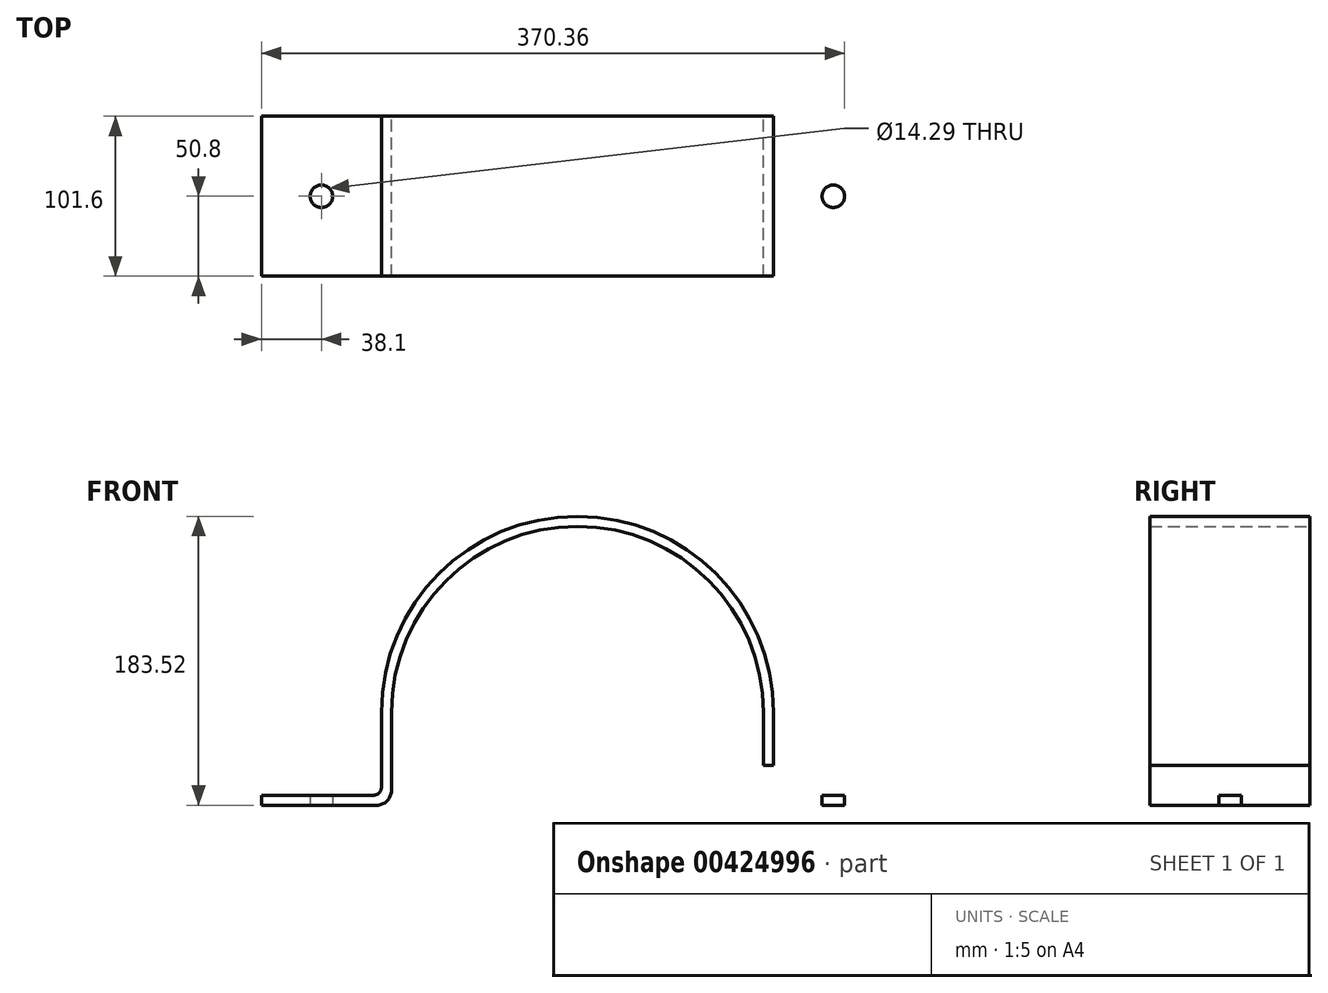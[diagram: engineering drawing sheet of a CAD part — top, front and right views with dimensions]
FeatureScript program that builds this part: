
annotation { "Feature Type Name" : "Feature", "Feature Type Description" : "" }
export const myFeature = defineFeature(function(context is Context, id is Id, definition is map)
    precondition{}
    {
        {
            var Q0;
            Q0=qCreatedBy(makeId("Front.planeOp"),FACE);
            var sketch = newSketch(context, id + "F0", { "sketchPlane" : qUnion([Q0])});
            skArc(sketch, "E0", {"start": v(118.11, 0) * mm, "mid": v(0, 118.11) * mm, "end": v(-118.11, 0) * mm});
            skArc(sketch, "E1", {"start": v(124.46, 0) * mm, "mid": v(0, 124.46) * mm, "end": v(-124.46, 0) * mm});
            skLineSegment(sketch, "E2", {"start": v(-118.11, 0) * mm, "end": v(-118.11, -59.06) * mm});
            skLineSegment(sketch, "E3", {"start": v(-118.11, -59.06) * mm, "end": v(-200.66, -59.06) * mm});
            skLineSegment(sketch, "E4", {"start": v(-200.66, -59.06) * mm, "end": v(-200.66, -52.7) * mm});
            skLineSegment(sketch, "E5", {"start": v(-200.66, -52.7) * mm, "end": v(-124.46, -52.7) * mm});
            skLineSegment(sketch, "E6", {"start": v(-124.46, -52.7) * mm, "end": v(-124.46, 0) * mm});
            skLineSegment(sketch, "E7.MirrorCS", {"start": v(124.46, -52.7) * mm, "end": v(124.46, 0) * mm});
            skLineSegment(sketch, "E8.MirrorCS", {"start": v(118.11, 0) * mm, "end": v(118.11, -59.06) * mm});
            skLineSegment(sketch, "E9.MirrorCS", {"start": v(118.11, -59.06) * mm, "end": v(200.66, -59.06) * mm});
            skLineSegment(sketch, "E10.MirrorCS", {"start": v(200.66, -52.7) * mm, "end": v(124.46, -52.7) * mm});
            skLineSegment(sketch, "E11.MirrorCS", {"start": v(200.66, -59.06) * mm, "end": v(200.66, -52.7) * mm});
            skPoint(sketch, "E12.end.orphan", {"position": v(-102.29, -59.06) * mm});
            skSolve(sketch);
        }
        {
            var Q0;
            Q0 = qSketchRegion(id + "F0", true);
            extrude(context, id + "F1", {"entities" : qUnion([Q0]), "endBound" : BoundingType.SYMMETRIC, "depth" : 101.6 * mm});
        }
        {
            var Q0;
            Q0=makeQuery(id+"F1.opExtrude","SWEPT_FACE",FACE,{"disambiguationData":[OSD([sQuery(id+"F0.wireOp",EDGE,"E9.MirrorCS")])]});
            var sketch = newSketch(context, id + "F2", { "sketchPlane" : qUnion([Q0])});
            skCircle(sketch, "E13", {"center": v(-162.56, 0) * mm, "radius": 7.14 * mm});
            skCircle(sketch, "E14.MirrorC", {"center": v(162.56, 0) * mm, "radius": 7.14 * mm});
            skSolve(sketch);
        }
        {
            var Q0;
            Q0=makeQuery(id+"F1.opExtrude","SWEPT_EDGE",EDGE,{"disambiguationData":[OSD([sQuery(id+"F0.wireOp",EDGE,"E2"),sQuery(id+"F0.wireOp",EDGE,"E3")])]});
            var Q1;
            Q1=makeQuery(id+"F1.opExtrude","SWEPT_EDGE",EDGE,{"disambiguationData":[OSD([sQuery(id+"F0.wireOp",EDGE,"E8.MirrorCS"),sQuery(id+"F0.wireOp",EDGE,"E9.MirrorCS")])]});
            fillet(context, id + "F3", {"entities" : qUnion([Q0, Q1]), "radius" : 9.52 * mm, "tangentPropagation" : true, "allowEdgeOverflow" : false});
        }
        {
            var Q0;
            Q0=makeQuery(id+"F1.opExtrude","SWEPT_EDGE",EDGE,{"disambiguationData":[OSD([sQuery(id+"F0.wireOp",EDGE,"E5"),sQuery(id+"F0.wireOp",EDGE,"E6")])]});
            var Q1;
            Q1=makeQuery(id+"F1.opExtrude","SWEPT_EDGE",EDGE,{"disambiguationData":[OSD([sQuery(id+"F0.wireOp",EDGE,"E7.MirrorCS"),sQuery(id+"F0.wireOp",EDGE,"E10.MirrorCS")])]});
            fillet(context, id + "F4", {"entities" : qUnion([Q0, Q1]), "radius" : 5.08 * mm, "tangentPropagation" : true, "allowEdgeOverflow" : false});
        }
        {
            var Q0;
            Q0=makeQuery(id+"F2.imprint","IMPRINT",FACE,{"disambiguationData":[TD([[makeQuery(id+"F2.imprint","IMPRINT",EDGE,{"derivedFrom":sQuery(id+"F2.wireOp",EDGE,"E13")}),1.0]])]});
            var Q1;
            Q1=makeQuery(id+"F2.imprint","IMPRINT",FACE,{"disambiguationData":[TD([[makeQuery(id+"F2.imprint","IMPRINT",EDGE,{"derivedFrom":sQuery(id+"F2.wireOp",EDGE,"E14.MirrorC")}),-1.0]])]});
            var Q2;
            Q2=sQuery(id+"F2.wireOp",EDGE,"E13");
            var Q3;
            Q3=sQuery(id+"F2.wireOp",EDGE,"E14.MirrorC");
            extrude(context, id + "F5", {"entities" : qUnion([Q0, Q1]), "operationType" : NewBodyOperationType.REMOVE, "surfaceEntities" : qUnion([Q2, Q3]), "oppositeDirection" : true, "depth" : 25.4 * mm});
        }
    });
